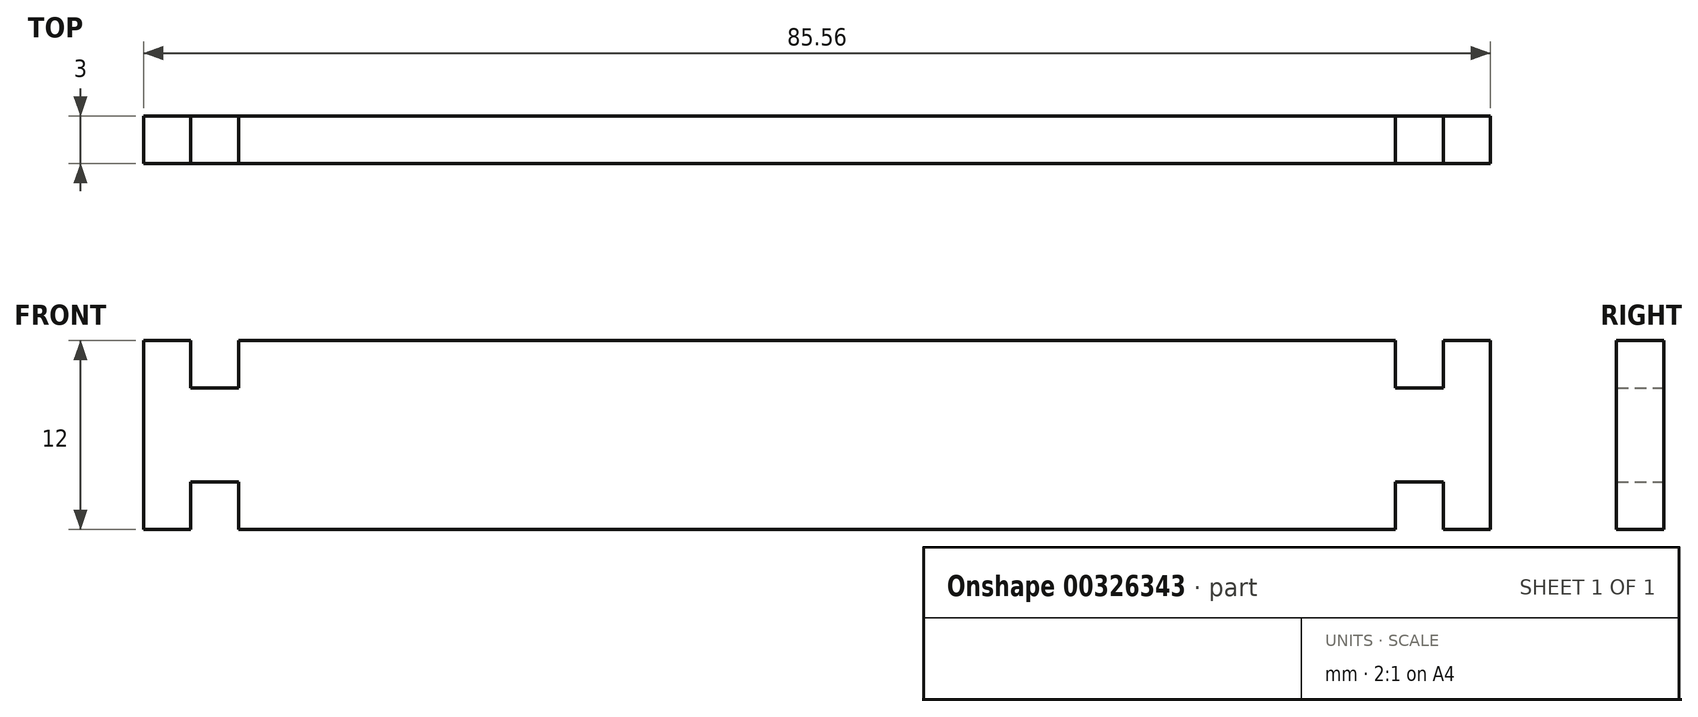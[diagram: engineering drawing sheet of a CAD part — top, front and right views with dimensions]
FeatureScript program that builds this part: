
annotation { "Feature Type Name" : "Feature", "Feature Type Description" : "" }
export const myFeature = defineFeature(function(context is Context, id is Id, definition is map)
    precondition{}
    {
        {
            var Q0;
            Q0=qCreatedBy(makeId("Front.planeOp"),FACE);
            var sketch = newSketch(context, id + "F0", { "sketchPlane" : qUnion([Q0])});
            skPoint(sketch, "E0", {"position": v(-39.78, 0) * mm});
            skPoint(sketch, "E1", {"position": v(-39.78, 3.02) * mm});
            skPoint(sketch, "E2", {"position": v(-36.74, 3.02) * mm});
            skPoint(sketch, "E3", {"position": v(39.78, 0) * mm});
            skPoint(sketch, "E4", {"position": v(39.78, 3.02) * mm});
            skPoint(sketch, "E5", {"position": v(36.74, 3.02) * mm});
            skPoint(sketch, "E6", {"position": v(36.74, 0) * mm});
            skLineSegment(sketch, "E7", {"start": v(-39.78, 0) * mm, "end": v(-39.78, 3.02) * mm});
            skLineSegment(sketch, "E8", {"start": v(-36.74, 3.02) * mm, "end": v(-39.78, 3.02) * mm});
            skLineSegment(sketch, "E9", {"start": v(-36.74, 0) * mm, "end": v(-36.74, 3.02) * mm});
            skLineSegment(sketch, "E10", {"start": v(36.74, 0) * mm, "end": v(36.74, 3.02) * mm});
            skLineSegment(sketch, "E11", {"start": v(39.78, 3.02) * mm, "end": v(36.74, 3.02) * mm});
            skLineSegment(sketch, "E12", {"start": v(39.78, 0) * mm, "end": v(39.78, 3.02) * mm});
            skLineSegment(sketch, "E13.trimOffspring", {"start": v(39.78, 0) * mm, "end": v(42.78, 0) * mm});
            skLineSegment(sketch, "E14.trimOffspring", {"start": v(-39.78, 0) * mm, "end": v(-42.78, 0) * mm});
            skLineSegment(sketch, "E15", {"start": v(-42.78, 12) * mm, "end": v(-39.78, 12) * mm});
            skLineSegment(sketch, "E16", {"start": v(-39.78, 12) * mm, "end": v(-39.78, 8.98) * mm});
            skLineSegment(sketch, "E17", {"start": v(-39.78, 8.98) * mm, "end": v(-36.74, 8.98) * mm});
            skLineSegment(sketch, "E18", {"start": v(-36.74, 8.98) * mm, "end": v(-36.74, 12) * mm});
            skLineSegment(sketch, "E19", {"start": v(42.78, 12) * mm, "end": v(39.78, 12) * mm});
            skLineSegment(sketch, "E20", {"start": v(39.78, 12) * mm, "end": v(39.78, 8.98) * mm});
            skLineSegment(sketch, "E21", {"start": v(39.78, 8.98) * mm, "end": v(36.74, 8.98) * mm});
            skLineSegment(sketch, "E22", {"start": v(36.74, 8.98) * mm, "end": v(36.74, 12) * mm});
            skLineSegment(sketch, "E23", {"start": v(36.74, 12) * mm, "end": v(-36.74, 12) * mm});
            skLineSegment(sketch, "E24", {"start": v(42.78, 12) * mm, "end": v(42.78, 0) * mm});
            skLineSegment(sketch, "E25", {"start": v(-42.78, 12) * mm, "end": v(-42.78, 0) * mm});
            skLineSegment(sketch, "E26", {"start": v(-36.74, 0) * mm, "end": v(36.74, 0) * mm});
            skSolve(sketch);
        }
        {
            var Q0;
            Q0=makeQuery(id+"F0.imprint","IMPRINT",FACE,{"disambiguationData":[TD([[makeQuery(id+"F0.imprint","IMPRINT",EDGE,{"derivedFrom":sQuery(id+"F0.wireOp",EDGE,"E7")}),1.0]])]});
            extrude(context, id + "F1", {"entities" : qUnion([Q0]), "depth" : 3 * mm});
        }
    });
